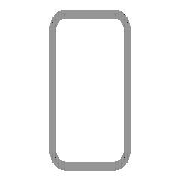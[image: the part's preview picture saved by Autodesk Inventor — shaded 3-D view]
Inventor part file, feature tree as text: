
AUTODESK INVENTOR PART (.ipt)
format: ipt  version: 2025 (Build 290162010, 162A)  size: 148,480 bytes
history: native  units: mm (DEFAULTED — no unit token found)
features: other x3, sketch x2, extrude x1, plane x1
ambient origin geometry x8: Origin, YZ Plane, XZ Plane, XY Plane, X Axis, Y Axis, Z Axis, Center Point
bodies: Solid1 (feature_tree), Body (feature_tree)
feature tree (7):
  other  "Driven Length"
  other  "Start plane"
  other  "End plane"
  extrude  "Extrusion2"  TaperAngle=0.0deg  [1 undecoded]
  sketch  "Sketch3"  dims[d3=180.0mm d4=0.0mm]
  plane  "Work Plane3"
  sketch  "Sketch5"  dims[d7=4.0mm d9=20.0mm d11=40.0mm d12=2.0mm d13=-0.0mm d14=180.0mm d15=10.0mm d16=20.0mm d17=90.0deg d18=180.0mm d19=45.0deg d20=0.0mm d21=0.0mm]
note: 1 required parameter value undecoded (feature->parameter linkage not recoverable at this tier; creation-order binding heuristic only, values carry confidence <= 0.55)
